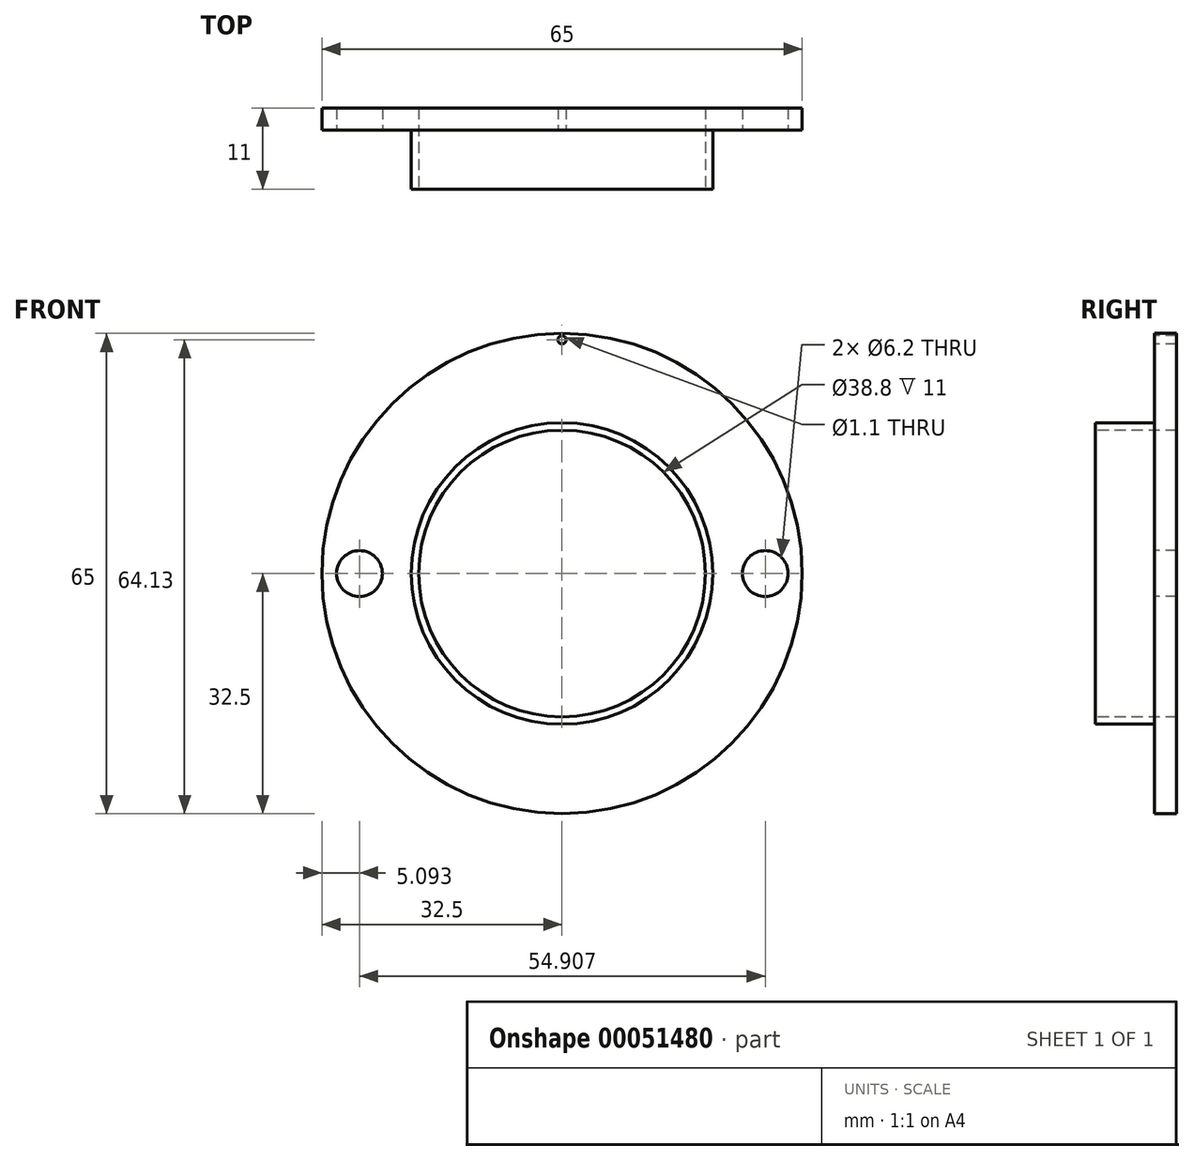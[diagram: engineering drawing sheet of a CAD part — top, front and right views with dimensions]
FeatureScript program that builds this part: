
annotation { "Feature Type Name" : "Feature", "Feature Type Description" : "" }
export const myFeature = defineFeature(function(context is Context, id is Id, definition is map)
    precondition{}
    {
        {
            var Q0;
            Q0=qCreatedBy(makeId("Front.planeOp"),FACE);
            var sketch = newSketch(context, id + "F0", { "sketchPlane" : qUnion([Q0])});
            skCircle(sketch, "E0", {"center": v(0, 0) * mm, "radius": 32.5 * mm});
            skSolve(sketch);
        }
        {
            var Q0;
            Q0=qSketchRegion(id+"F0",true);
            extrude(context, id + "F1", {"entities" : qUnion([Q0]), "depth" : 3 * mm});
        }
        {
            var Q0;
            Q0=makeQuery(id+"F1.opExtrude","CAP_FACE",FACE,{"disambiguationData":[OSD([sQuery(id+"F0.wireOp",EDGE,"E0")])],"isStart":false});
            var sketch = newSketch(context, id + "F2", { "sketchPlane" : qUnion([Q0])});
            skCircle(sketch, "E1", {"center": v(0, 0) * mm, "radius": 20.4 * mm});
            skSolve(sketch);
        }
        {
            var Q0;
            Q0 = qSketchRegion(id + "F2", true);
            extrude(context, id + "F3", {"entities" : qUnion([Q0]), "operationType" : NewBodyOperationType.ADD, "depth" : 8 * mm});
        }
        {
            var Q0;
            Q0=makeQuery(id+"F3.opExtrude","CAP_FACE",FACE,{"disambiguationData":[OSD([sQuery(id+"F2.wireOp",EDGE,"E1")])],"isStart":false});
            var sketch = newSketch(context, id + "F4", { "sketchPlane" : qUnion([Q0])});
            skCircle(sketch, "E2", {"center": v(0, 0) * mm, "radius": 19.4 * mm});
            skSolve(sketch);
        }
        {
            var Q0;
            Q0 = qSketchRegion(id + "F4", true);
            extrude(context, id + "F5", {"entities" : qUnion([Q0]), "operationType" : NewBodyOperationType.REMOVE, "endBound" : BoundingType.THROUGH_ALL, "oppositeDirection" : true, "depth" : 25 * mm});
        }
        {
            var Q0;
            Q0=makeQuery(id+"F2.imprint","IMPRINT",FACE,{"disambiguationData":[TD([[makeQuery(id+"F2.imprint","IMPRINT",EDGE,{"derivedFrom":sQuery(id+"F2.wireOp",EDGE,"E1")}),-1.0]])]});
            var sketch = newSketch(context, id + "F6", { "sketchPlane" : qUnion([Q0])});
            skCircle(sketch, "E3", {"center": v(27.5, 0) * mm, "radius": 3.1 * mm});
            skCircle(sketch, "E4", {"center": v(-27.4, 0) * mm, "radius": 3.1 * mm});
            skCircle(sketch, "E5", {"center": v(0, 31.63) * mm, "radius": 0.55 * mm});
            skSolve(sketch);
        }
        {
            var Q0;
            Q0 = qSketchRegion(id + "F6", true);
            extrude(context, id + "F7", {"entities" : qUnion([Q0]), "operationType" : NewBodyOperationType.REMOVE, "endBound" : BoundingType.THROUGH_ALL, "oppositeDirection" : true, "depth" : 25 * mm});
        }
    });
